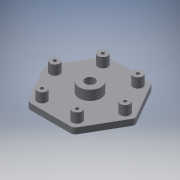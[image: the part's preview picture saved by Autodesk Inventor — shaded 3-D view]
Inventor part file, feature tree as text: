
AUTODESK INVENTOR PART (.ipt)
format: ipt  version: 2017 (Build 210142000, 142)  size: 189,440 bytes
history: native  units: mm
features: extrude x4, sketch x4, projected_geometry x2, fillet x1
ambient origin geometry x8: Origin, YZ Plane, XZ Plane, XY Plane, X Axis, Y Axis, Z Axis, Center Point
bodies: Solid1 (feature_tree)
feature tree (11):
  extrude  "Extrusion1"  Depth=8.0mm
  fillet  "Fillet1"  Radius=8.0mm
  extrude  "Extrusion2"  Depth=8.0mm
  extrude  "Extrusion3"  Depth=4.0mm
  extrude  "Extrusion4"  Depth=8.0mm TaperAngle=0.0deg
  sketch  "Sketch1"  dims[d0=22.0mm d1=50.229473mm d2=8.0mm]
  sketch  "Sketch2"  dims[d3=65.0mm d4=8.0mm]
  projected_geometry  "Projected Loop1"
  sketch  "Sketch3"  dims[d5=5.0mm d6=0.0mm d7=4.0mm]
  projected_geometry  "Projected Loop2"
  sketch  "Sketch4"  dims[d8=5.0mm d9=8.0mm d10=0.0mm d11=8.0mm d12=0.0mm d13=80.0mm d14=2.7mm d15=10.0mm d16=0.0mm d17=75.055535mm]
